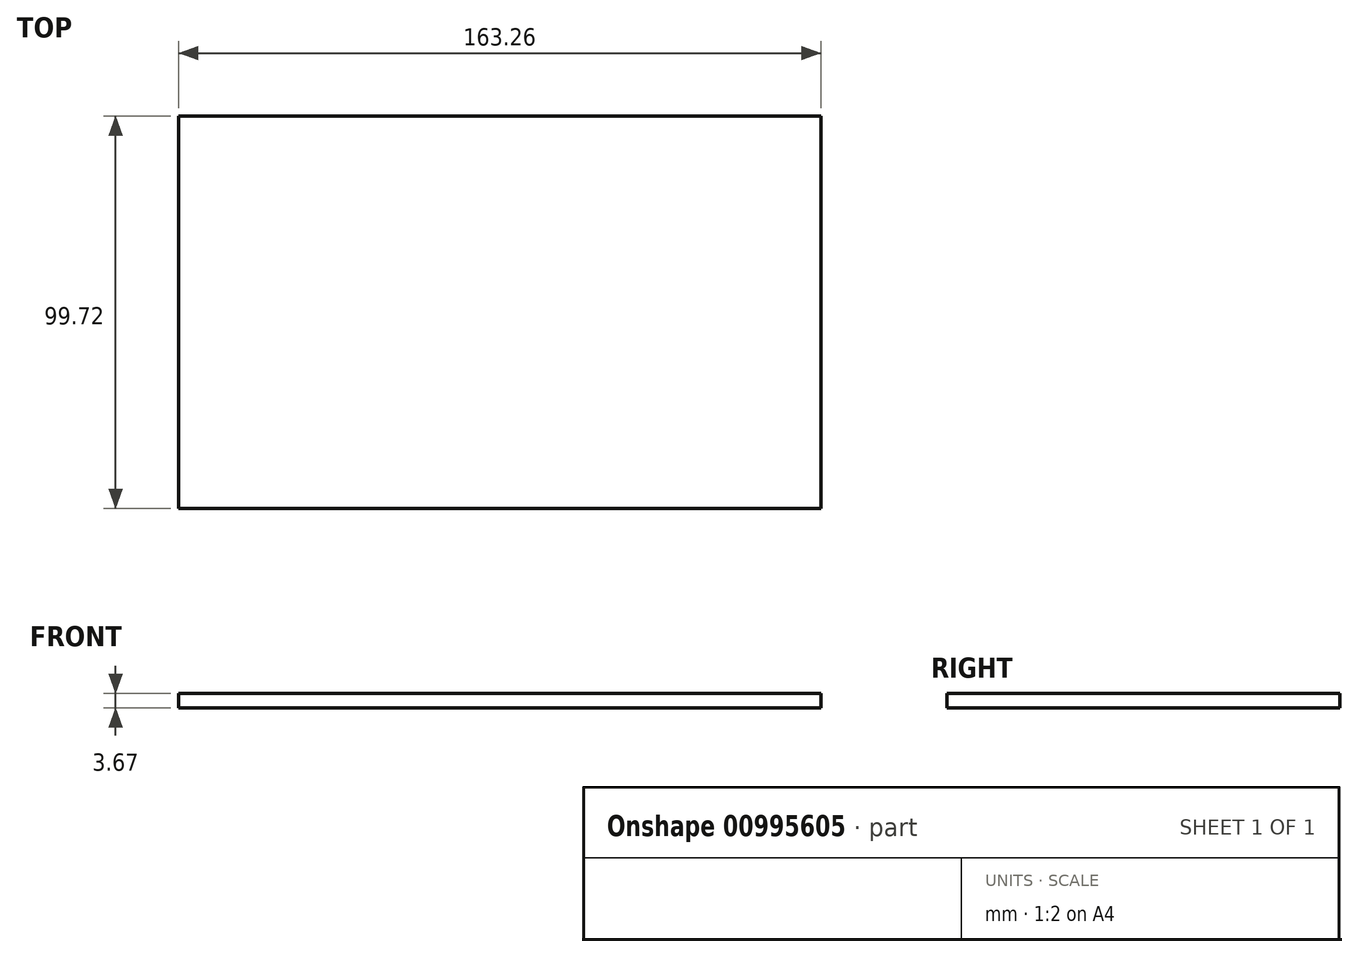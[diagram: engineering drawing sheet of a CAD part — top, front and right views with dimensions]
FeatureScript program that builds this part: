
annotation { "Feature Type Name" : "Feature", "Feature Type Description" : "" }
export const myFeature = defineFeature(function(context is Context, id is Id, definition is map)
    precondition{}
    {
        {
            var Q0;
            Q0=qCreatedBy(makeId("Top.planeOp"),FACE);
            var sketch = newSketch(context, id + "F0", { "sketchPlane" : qUnion([Q0])});
            skLineSegment(sketch, "E0.bottom", {"start": v(81.63, 49.86) * mm, "end": v(-81.63, 49.86) * mm});
            skLineSegment(sketch, "E0.top", {"start": v(81.63, -49.86) * mm, "end": v(-81.63, -49.86) * mm});
            skLineSegment(sketch, "E0.left", {"start": v(81.63, 49.86) * mm, "end": v(81.63, -49.86) * mm});
            skLineSegment(sketch, "E0.right", {"start": v(-81.63, 49.86) * mm, "end": v(-81.63, -49.86) * mm});
            skPoint(sketch, "E0.middle", {"position": v(0, 0) * mm});
            skSolve(sketch);
        }
        {
            var Q0;
            Q0=makeQuery(id+"F0.imprint","IMPRINT",FACE,{"disambiguationData":[TD([[makeQuery(id+"F0.imprint","IMPRINT",EDGE,{"derivedFrom":sQuery(id+"F0.wireOp",EDGE,"E0.bottom")}),1.0]])]});
            extrude(context, id + "F1", {"entities" : qUnion([Q0]), "depth" : 3.67 * mm, "offsetDistance" : 25.4 * mm});
        }
    });
